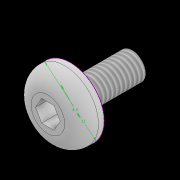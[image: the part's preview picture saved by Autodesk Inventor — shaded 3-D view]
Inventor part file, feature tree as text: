
AUTODESK INVENTOR PART (.ipt)
format: ipt  version: 2022.2 (Build 262287010, 287A)  size: 133,120 bytes
history: native  units: mm
features: extrude x3, sketch x2, fillet x2, thread x1
ambient origin geometry x8: Origin, YZ Plane, XZ Plane, XY Plane, X Axis, Y Axis, Z Axis, Center Point
bodies: Solid1 (feature_tree)
feature tree (8):
  sketch  "Sketch1"  dims[d0=4.8mm d1=12.0mm]
  extrude  "Extrusion1"  Depth=12.0mm
  extrude  "Extrusion2"  Depth=11.0mm TaperAngle=0.0deg
  fillet  "Fillet1"  Radius=1.0mm
  fillet  "Fillet2"  Radius=3.0mm
  extrude  "Extrusion3"  Depth=10.0mm
  thread  "Thread1"  [1 undecoded]
  sketch  "Sketch2"  dims[d2=4.0mm d3=0.0mm d4=11.0mm d5=0.0mm d6=1.0mm d7=3.0mm d8=4.4mm d9=3.0mm d10=0.0mm d11=10.0mm d12=0.0mm]
note: 1 required parameter value undecoded (feature->parameter linkage not recoverable at this tier; creation-order binding heuristic only, values carry confidence <= 0.55)
